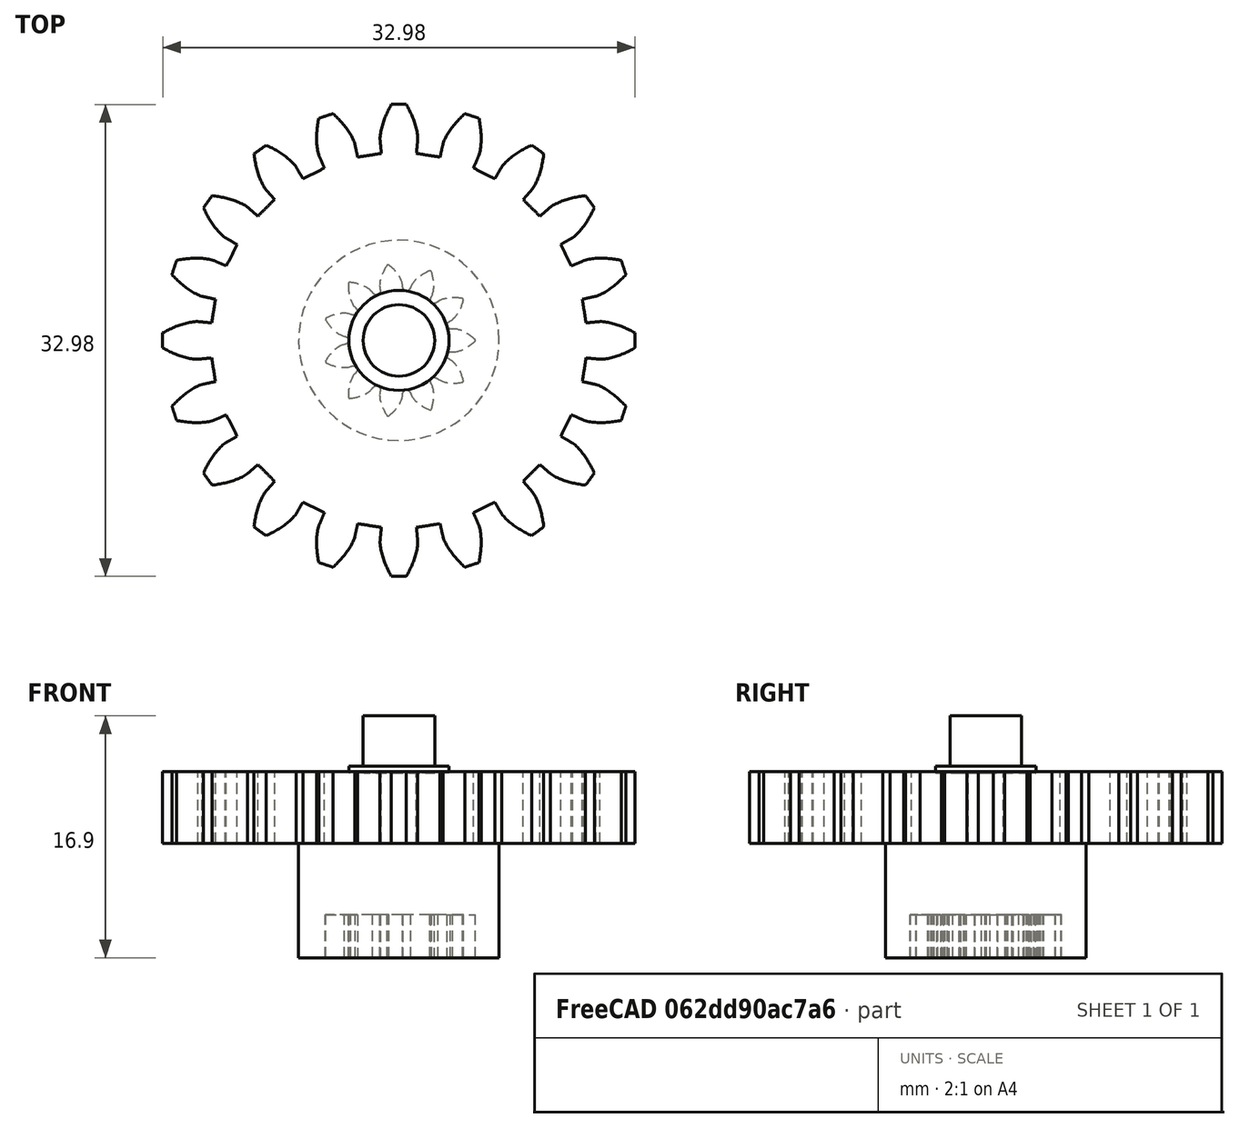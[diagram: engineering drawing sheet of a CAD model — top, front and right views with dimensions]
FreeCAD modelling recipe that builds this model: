
FCSTD DOCUMENT  (FreeCAD 0.19R24291 (Git))
Label: Blind cog shaft
License: All rights reserved
LicenseURL: http://en.wikipedia.org/wiki/All_rights_reserved
objects: PartDesign::Body×4, PartDesign::AdditiveCylinder×3, PartDesign::FeaturePython×2, Part::Cut×1, App::Part×1
note: 13 computed .brp shape members not serialized (recipe doc carries the construction recipe); baked Part::Feature solids carry a one-line shape summary decoded from their .brp

FEATURE [PartDesign::AdditiveCylinder] Cylinder001
  Angle = 360
  AttacherType = Attacher::AttachEngine3D
  Height = 8
  Radius = 7
FEATURE [PartDesign::Body] Body
  Group = -> [Cylinder001]
  Origin = -> Origin001
  Tip = -> Cylinder001
FEATURE [PartDesign::FeaturePython] involutegear  # WARN: FeaturePython — macro-defined, semantics opaque (R4)
  AttacherType = Attacher::AttachEngine3D
  backlash = 0
  beta = 0
  clearance = 0.25
  da = 10.66
  df = 6.97
  double_helix = false
  dw = 9.02
  head = 0
  height = 3
  module = 0.82
  numpoints = 8
  pressure_angle = 32
  properties_from_tool = false
  reversed_backlash = false
  shift = 0
  simple = false
  teeth = 11
  transverse_pitch = 2.57611
  undercut = true
  version = 0.0.3
FEATURE [PartDesign::Body] Body001
  Group = -> [involutegear]
  Origin = -> Origin002
  Tip = -> involutegear
FEATURE [Part::Cut] Cut
  Base = -> Body
  Tool = -> Body001
FEATURE [PartDesign::FeaturePython] involutegear002  # WARN: FeaturePython — macro-defined, semantics opaque (R4)
  AttacherType = Attacher::AttachEngine3D
  backlash = 0
  beta = 0
  clearance = 0.25
  da = 33
  df = 26.25
  double_helix = false
  dw = 30
  head = 0
  height = 5
  module = 1.5
  numpoints = 6
  pressure_angle = 20
  properties_from_tool = false
  reversed_backlash = false
  shift = 0
  simple = false
  teeth = 20
  transverse_pitch = 4.71239
  undercut = false
  version = 0.0.3
FEATURE [PartDesign::Body] Body002
  Group = -> [involutegear002]
  Origin = -> Origin003
  Placement = pos=(0,0,8) rot=(0,0,1;0rad)
  Tip = -> involutegear002
FEATURE [PartDesign::AdditiveCylinder] Cylinder
  Angle = 360
  AttacherType = Attacher::AttachEngine3D
  Height = 0.5
  Radius = 3.5
FEATURE [PartDesign::AdditiveCylinder] Cylinder002
  Angle = 360
  AttacherType = Attacher::AttachEngine3D
  BaseFeature = -> Cylinder
  Height = 4
  Radius = 2.5
FEATURE [PartDesign::Body] Body003
  Group = -> [Cylinder,Cylinder002]
  Origin = -> Origin004
  Placement = pos=(0,0,12.9) rot=(0,0,1;0rad)
  Tip = -> Cylinder002
FEATURE [App::Part] Part  label="Blind cog housing"
  Group = -> [Body,Body001,Body002,Body003,Cut]
  Origin = -> Origin
